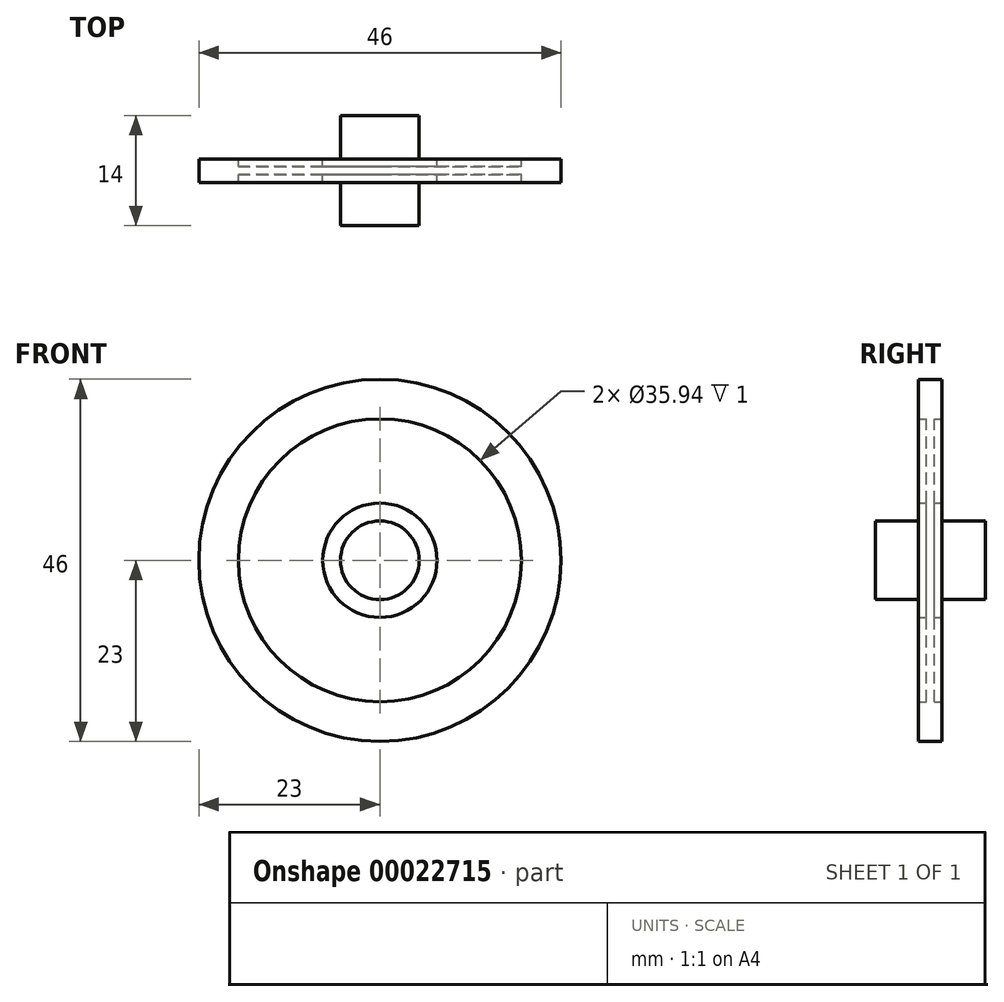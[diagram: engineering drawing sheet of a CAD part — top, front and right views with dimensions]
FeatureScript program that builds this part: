
annotation { "Feature Type Name" : "Feature", "Feature Type Description" : "" }
export const myFeature = defineFeature(function(context is Context, id is Id, definition is map)
    precondition{}
    {
        {
            var Q0;
            Q0=qCreatedBy(makeId("Front.planeOp"),FACE);
            var sketch = newSketch(context, id + "F0", { "sketchPlane" : qUnion([Q0])});
            skCircle(sketch, "E0", {"center": v(0, 0) * mm, "radius": 23 * mm});
            skCircle(sketch, "E1", {"center": v(0, 0) * mm, "radius": 17.97 * mm});
            skCircle(sketch, "E2", {"center": v(0, 0) * mm, "radius": 7.26 * mm});
            skCircle(sketch, "E3", {"center": v(0, 0) * mm, "radius": 5 * mm});
            skSolve(sketch);
        }
        {
            var Q0;
            Q0=makeQuery(id+"F0.imprint","IMPRINT",FACE,{"disambiguationData":[TD([[makeQuery(id+"F0.imprint","IMPRINT",EDGE,{"derivedFrom":sQuery(id+"F0.wireOp",EDGE,"E0")}),1.0]])]});
            extrude(context, id + "F1", {"entities" : qUnion([Q0]), "depth" : 1.5 * mm, "hasSecondDirection" : true, "secondDirectionOppositeDirection" : true, "secondDirectionDepth" : 1.5 * mm});
        }
        {
            var Q0;
            Q0=makeQuery(id+"F0.imprint","IMPRINT",FACE,{"disambiguationData":[TD([[makeQuery(id+"F0.imprint","IMPRINT",EDGE,{"derivedFrom":sQuery(id+"F0.wireOp",EDGE,"E1")}),1.0]])]});
            extrude(context, id + "F2", {"entities" : qUnion([Q0]), "operationType" : NewBodyOperationType.ADD, "depth" : .5 * mm, "hasSecondDirection" : true, "secondDirectionOppositeDirection" : true, "secondDirectionDepth" : .5 * mm});
        }
        {
            var Q0;
            Q0=makeQuery(id+"F0.imprint","IMPRINT",FACE,{"disambiguationData":[TD([[makeQuery(id+"F0.imprint","IMPRINT",EDGE,{"derivedFrom":sQuery(id+"F0.wireOp",EDGE,"E2")}),1.0]])]});
            extrude(context, id + "F3", {"entities" : qUnion([Q0]), "operationType" : NewBodyOperationType.ADD, "depth" : 1.5 * mm, "hasSecondDirection" : true, "secondDirectionOppositeDirection" : true, "secondDirectionDepth" : 1.5 * mm});
        }
        {
            var Q0;
            Q0=makeQuery(id+"F0.imprint","IMPRINT",FACE,{"disambiguationData":[TD([[makeQuery(id+"F0.imprint","IMPRINT",EDGE,{"derivedFrom":sQuery(id+"F0.wireOp",EDGE,"E3")}),1.0]])]});
            extrude(context, id + "F4", {"entities" : qUnion([Q0]), "operationType" : NewBodyOperationType.ADD, "endBound" : BoundingType.SYMMETRIC, "depth" : 14 * mm});
        }
    });
